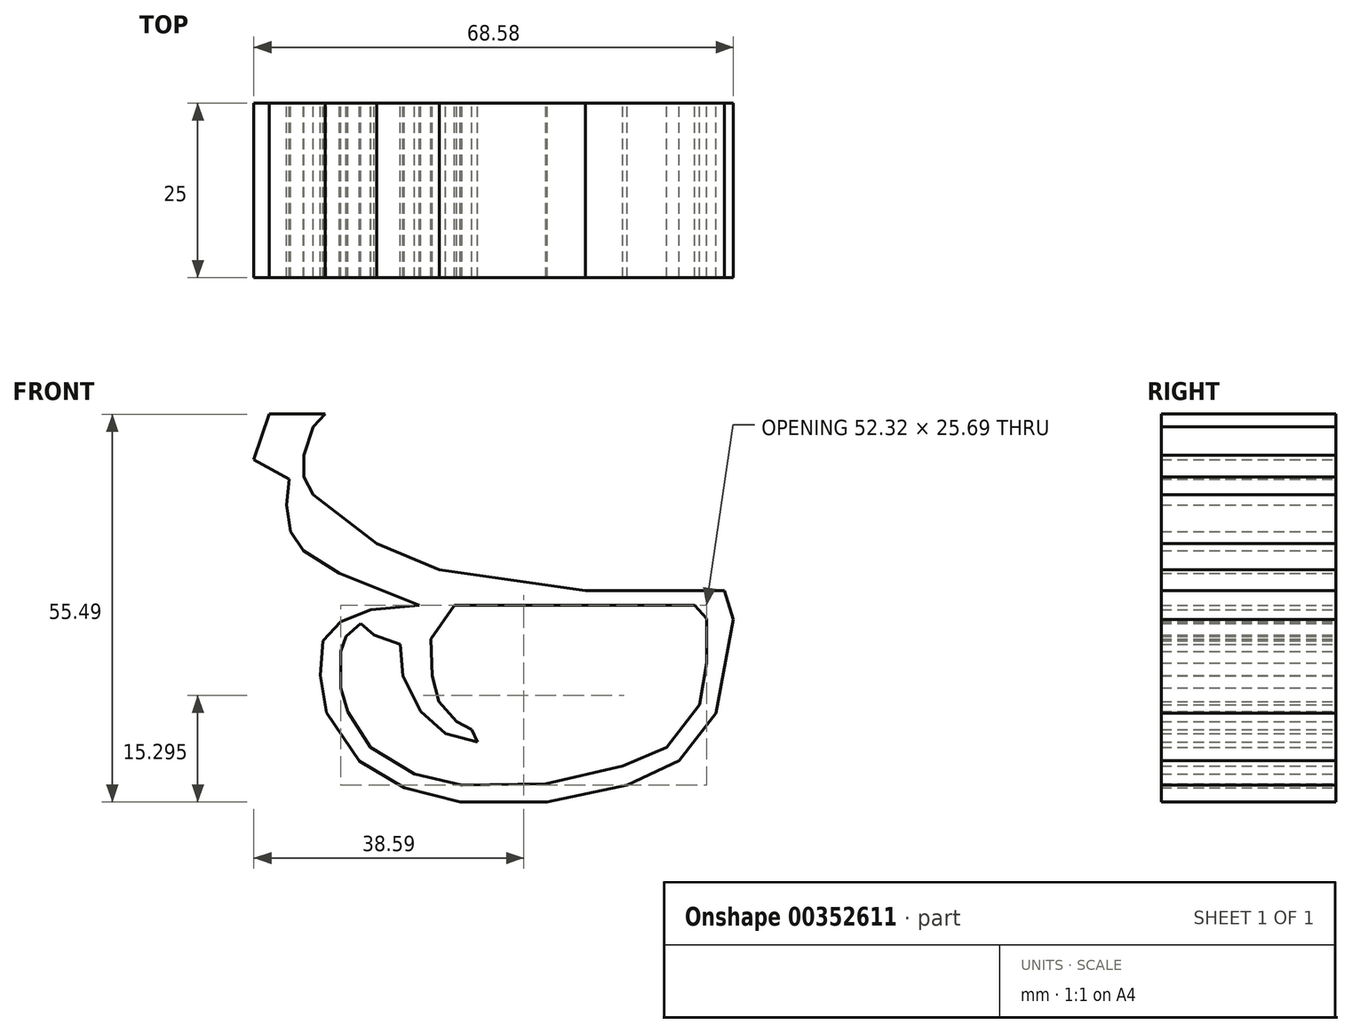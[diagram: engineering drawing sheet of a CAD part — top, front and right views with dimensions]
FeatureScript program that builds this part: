
annotation { "Feature Type Name" : "Feature", "Feature Type Description" : "" }
export const myFeature = defineFeature(function(context is Context, id is Id, definition is map)
    precondition{}
    {
        {
            var Q0;
            Q0=qCreatedBy(makeId("Front.planeOp"),FACE);
            var sketch = newSketch(context, id + "F0", { "sketchPlane" : qUnion([Q0])});
            skLineSegment(sketch, "E0", {"start": v(-56.58, -4.03) * mm, "end": v(-59.13, -6.77) * mm});
            skLineSegment(sketch, "E1", {"start": v(-59.13, -6.77) * mm, "end": v(-59.48, -11.72) * mm});
            skLineSegment(sketch, "E2", {"start": v(-59.48, -11.72) * mm, "end": v(-58.62, -17.03) * mm});
            skLineSegment(sketch, "E3", {"start": v(-58.62, -17.03) * mm, "end": v(-53.9, -23.97) * mm});
            skLineSegment(sketch, "E4", {"start": v(-53.9, -23.97) * mm, "end": v(-47.53, -27.77) * mm});
            skLineSegment(sketch, "E5", {"start": v(-47.53, -27.77) * mm, "end": v(-39.49, -29.84) * mm});
            skLineSegment(sketch, "E6", {"start": v(-39.49, -29.84) * mm, "end": v(-27.07, -29.84) * mm});
            skLineSegment(sketch, "E7", {"start": v(-27.07, -29.84) * mm, "end": v(-15.62, -27.37) * mm});
            skLineSegment(sketch, "E8", {"start": v(-15.62, -27.37) * mm, "end": v(-8.18, -23.9) * mm});
            skLineSegment(sketch, "E9", {"start": v(-8.18, -23.9) * mm, "end": v(-2.9, -17.13) * mm});
            skLineSegment(sketch, "E10", {"start": v(-2.9, -17.13) * mm, "end": v(-0.43, -3.74) * mm});
            skLineSegment(sketch, "E11", {"start": v(-0.43, -3.74) * mm, "end": v(-1.7, 0.43) * mm});
            skLineSegment(sketch, "E12", {"start": v(-1.7, 0.43) * mm, "end": v(-21.6, 0.43) * mm});
            skLineSegment(sketch, "E13", {"start": v(-21.6, 0.43) * mm, "end": v(-42.48, 3.42) * mm});
            skLineSegment(sketch, "E14", {"start": v(-42.48, 3.42) * mm, "end": v(-51.46, 7.15) * mm});
            skLineSegment(sketch, "E15", {"start": v(-51.46, 7.15) * mm, "end": v(-60.5, 14.14) * mm});
            skLineSegment(sketch, "E16", {"start": v(-60.5, 14.14) * mm, "end": v(-61.86, 16.68) * mm});
            skLineSegment(sketch, "E17", {"start": v(-61.86, 16.68) * mm, "end": v(-61.86, 19.78) * mm});
            skLineSegment(sketch, "E18", {"start": v(-61.86, 19.78) * mm, "end": v(-60.5, 23.83) * mm});
            skLineSegment(sketch, "E19", {"start": v(-60.5, 23.83) * mm, "end": v(-58.82, 25.65) * mm});
            skLineSegment(sketch, "E20", {"start": v(-58.82, 25.65) * mm, "end": v(-66.82, 25.65) * mm});
            skLineSegment(sketch, "E21", {"start": v(-66.82, 25.65) * mm, "end": v(-69.01, 19.17) * mm});
            skLineSegment(sketch, "E22", {"start": v(-69.01, 19.17) * mm, "end": v(-63.93, 16.36) * mm});
            skLineSegment(sketch, "E23", {"start": v(-63.93, 16.36) * mm, "end": v(-64.35, 12.66) * mm});
            skLineSegment(sketch, "E24", {"start": v(-64.35, 12.66) * mm, "end": v(-63.79, 8.87) * mm});
            skLineSegment(sketch, "E25", {"start": v(-63.79, 8.87) * mm, "end": v(-61.94, 6.14) * mm});
            skLineSegment(sketch, "E26", {"start": v(-61.94, 6.14) * mm, "end": v(-56.8, 2.86) * mm});
            skLineSegment(sketch, "E27", {"start": v(-56.8, 2.86) * mm, "end": v(-45.35, -1.67) * mm});
            skLineSegment(sketch, "E28", {"start": v(-45.35, -1.67) * mm, "end": v(-52.28, -2.3) * mm});
            skLineSegment(sketch, "E29", {"start": v(-52.28, -2.3) * mm, "end": v(-56.58, -4.03) * mm});
            skLineSegment(sketch, "E30", {"start": v(-56.58, -8.31) * mm, "end": v(-56.58, -13.47) * mm});
            skLineSegment(sketch, "E31", {"start": v(-56.58, -13.47) * mm, "end": v(-55.6, -16.93) * mm});
            skLineSegment(sketch, "E32", {"start": v(-55.6, -16.93) * mm, "end": v(-52.32, -22.03) * mm});
            skLineSegment(sketch, "E33", {"start": v(-52.32, -22.03) * mm, "end": v(-46.05, -25.84) * mm});
            skLineSegment(sketch, "E34", {"start": v(-46.05, -25.84) * mm, "end": v(-39.28, -27.39) * mm});
            skLineSegment(sketch, "E35", {"start": v(-39.28, -27.39) * mm, "end": v(-27.28, -27.22) * mm});
            skLineSegment(sketch, "E36", {"start": v(-27.28, -27.22) * mm, "end": v(-16.24, -24.67) * mm});
            skLineSegment(sketch, "E37", {"start": v(-16.24, -24.67) * mm, "end": v(-9.95, -22.01) * mm});
            skLineSegment(sketch, "E38", {"start": v(-9.95, -22.01) * mm, "end": v(-5.31, -15.9) * mm});
            skLineSegment(sketch, "E39", {"start": v(-5.31, -15.9) * mm, "end": v(-4.26, -9.91) * mm});
            skLineSegment(sketch, "E40", {"start": v(-4.26, -9.91) * mm, "end": v(-4.26, -3.62) * mm});
            skLineSegment(sketch, "E41", {"start": v(-4.26, -3.62) * mm, "end": v(-6.01, -1.7) * mm});
            skLineSegment(sketch, "E42", {"start": v(-6.01, -1.7) * mm, "end": v(-40.31, -1.7) * mm});
            skLineSegment(sketch, "E43", {"start": v(-40.31, -1.7) * mm, "end": v(-43.7, -6.54) * mm});
            skLineSegment(sketch, "E44", {"start": v(-43.7, -6.54) * mm, "end": v(-43.52, -11.8) * mm});
            skLineSegment(sketch, "E45", {"start": v(-43.52, -11.8) * mm, "end": v(-42.56, -15.47) * mm});
            skLineSegment(sketch, "E46", {"start": v(-42.56, -15.47) * mm, "end": v(-40, -18.33) * mm});
            skLineSegment(sketch, "E47", {"start": v(-40, -18.33) * mm, "end": v(-37.86, -19.46) * mm});
            skLineSegment(sketch, "E48", {"start": v(-37.86, -19.46) * mm, "end": v(-37.06, -21.26) * mm});
            skLineSegment(sketch, "E49", {"start": v(-37.06, -21.26) * mm, "end": v(-41.61, -20.04) * mm});
            skLineSegment(sketch, "E50", {"start": v(-41.61, -20.04) * mm, "end": v(-45.15, -16.89) * mm});
            skLineSegment(sketch, "E51", {"start": v(-45.15, -16.89) * mm, "end": v(-47.69, -11.78) * mm});
            skLineSegment(sketch, "E52", {"start": v(-47.69, -11.78) * mm, "end": v(-48.1, -7.29) * mm});
            skLineSegment(sketch, "E53", {"start": v(-48.1, -7.29) * mm, "end": v(-51.84, -5.94) * mm});
            skLineSegment(sketch, "E54", {"start": v(-51.84, -5.94) * mm, "end": v(-53.76, -4.29) * mm});
            skLineSegment(sketch, "E55", {"start": v(-53.76, -4.29) * mm, "end": v(-55.83, -6.14) * mm});
            skLineSegment(sketch, "E56", {"start": v(-55.83, -6.14) * mm, "end": v(-56.58, -8.31) * mm});
            skSolve(sketch);
        }
        {
            var Q0;
            Q0=makeQuery(id+"F0.imprint","IMPRINT",FACE,{"disambiguationData":[TD([[makeQuery(id+"F0.imprint","IMPRINT",EDGE,{"derivedFrom":sQuery(id+"F0.wireOp",EDGE,"E0")}),1.0]])]});
            var Q1;
            Q1 = qSketchRegion(id + "F0", true);
            extrude(context, id + "F1", {"entities" : qUnion([Q0, Q1]), "endBound" : BoundingType.SYMMETRIC, "depth" : 25 * mm});
        }
    });
